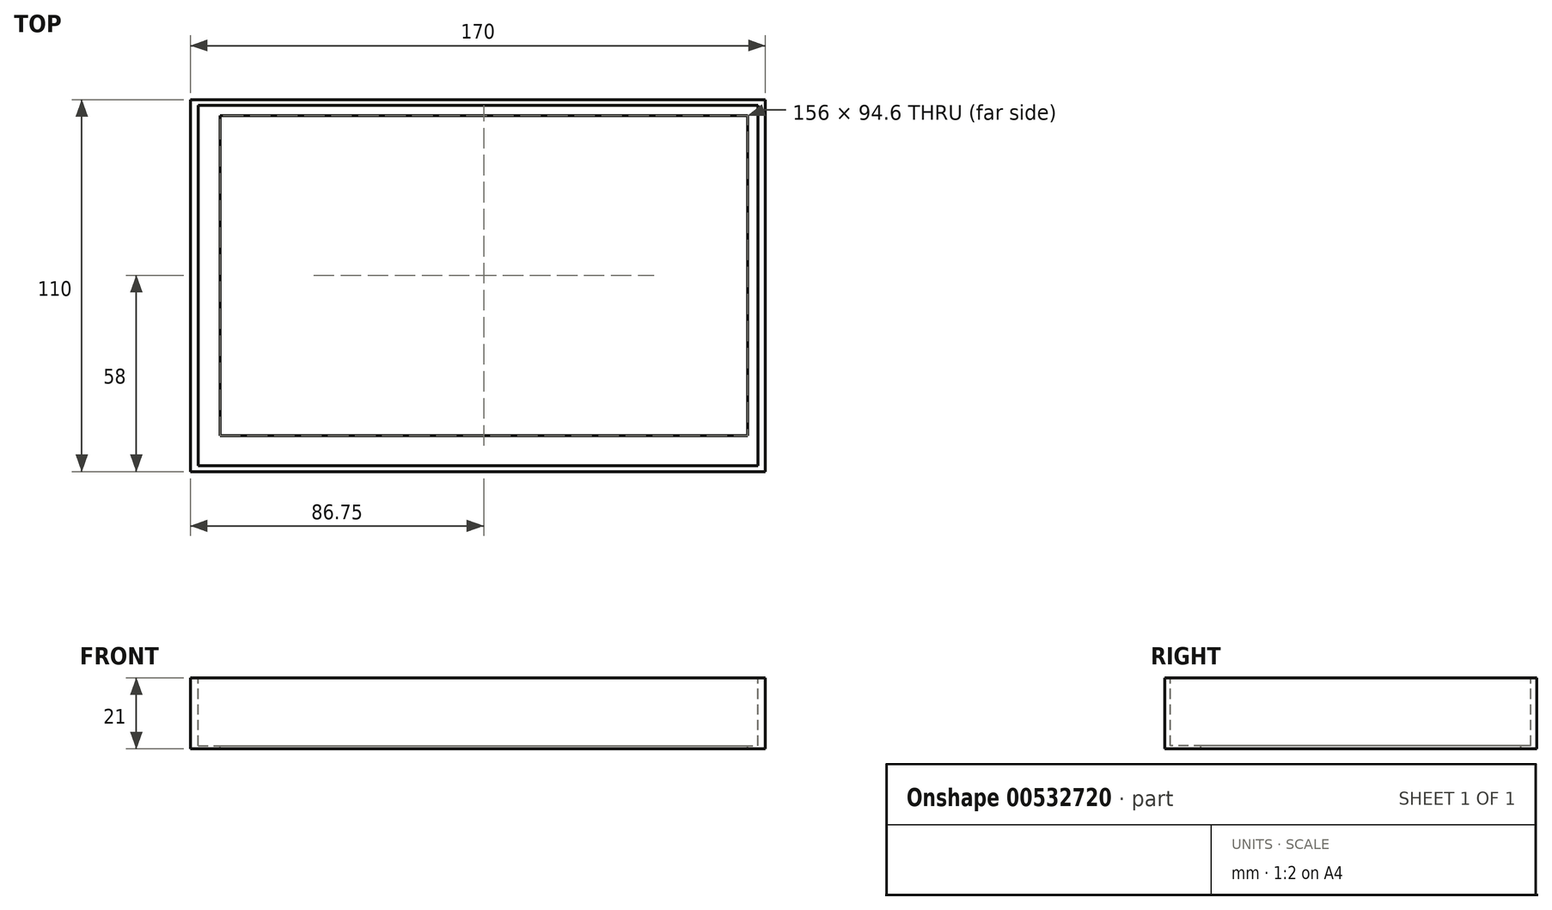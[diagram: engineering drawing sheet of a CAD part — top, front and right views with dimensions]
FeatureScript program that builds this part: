
annotation { "Feature Type Name" : "Feature", "Feature Type Description" : "" }
export const myFeature = defineFeature(function(context is Context, id is Id, definition is map)
    precondition{}
    {
        {
            var Q0;
            Q0=qCreatedBy(makeId("Top.planeOp"),FACE);
            var sketch = newSketch(context, id + "F0", { "sketchPlane" : qUnion([Q0])});
            skLineSegment(sketch, "E0.bottom", {"start": v(85, -55) * mm, "end": v(-85, -55) * mm});
            skLineSegment(sketch, "E0.top", {"start": v(85, 55) * mm, "end": v(-85, 55) * mm});
            skLineSegment(sketch, "E0.left", {"start": v(85, -55) * mm, "end": v(85, 55) * mm});
            skLineSegment(sketch, "E0.right", {"start": v(-85, -55) * mm, "end": v(-85, 55) * mm});
            skPoint(sketch, "E0.middle", {"position": v(0, 0) * mm});
            skSolve(sketch);
        }
        {
            var Q0;
            Q0=makeQuery(id+"F0.imprint","IMPRINT",FACE,{"disambiguationData":[TD([[makeQuery(id+"F0.imprint","IMPRINT",EDGE,{"derivedFrom":sQuery(id+"F0.wireOp",EDGE,"E0.bottom")}),-1.0]])]});
            extrude(context, id + "F1", {"entities" : qUnion([Q0]), "depth" : 21 * mm, "offsetDistance" : 25 * mm});
        }
        {
            var Q0;
            Q0=makeQuery(id+"F1.opExtrude","CAP_FACE",FACE,{"disambiguationData":[OSD([sQuery(id+"F0.wireOp",EDGE,"E0.bottom"),sQuery(id+"F0.wireOp",EDGE,"E0.top"),sQuery(id+"F0.wireOp",EDGE,"E0.left"),sQuery(id+"F0.wireOp",EDGE,"E0.right")])],"isStart":false});
            var sketch = newSketch(context, id + "F2", { "sketchPlane" : qUnion([Q0])});
            skLineSegment(sketch, "E1.bottom", {"start": v(-82.75, 53.3) * mm, "end": v(82.75, 53.3) * mm});
            skLineSegment(sketch, "E1.top", {"start": v(-82.75, -53.3) * mm, "end": v(82.75, -53.3) * mm});
            skLineSegment(sketch, "E1.left", {"start": v(-82.75, 53.3) * mm, "end": v(-82.75, -53.3) * mm});
            skLineSegment(sketch, "E1.right", {"start": v(82.75, 53.3) * mm, "end": v(82.75, -53.3) * mm});
            skSolve(sketch);
        }
        {
            var Q0;
            Q0=makeQuery(id+"F2.imprint","IMPRINT",FACE,{"disambiguationData":[TD([[makeQuery(id+"F2.imprint","IMPRINT",EDGE,{"derivedFrom":sQuery(id+"F2.wireOp",EDGE,"E1.bottom")}),-1.0]])]});
            extrude(context, id + "F3", {"entities" : qUnion([Q0]), "operationType" : NewBodyOperationType.REMOVE, "oppositeDirection" : true, "depth" : 20 * mm, "offsetDistance" : 25 * mm});
        }
        {
            var Q0;
            Q0=makeQuery(id+"F3.boolean.opBoolean","COPY",FACE,{"derivedFrom":makeQuery(id+"F3.opExtrude","CAP_FACE",FACE,{"disambiguationData":[OSD([sQuery(id+"F2.wireOp",EDGE,"E1.bottom"),sQuery(id+"F2.wireOp",EDGE,"E1.top"),sQuery(id+"F2.wireOp",EDGE,"E1.left"),sQuery(id+"F2.wireOp",EDGE,"E1.right")])],"isStart":false})});
            var sketch = newSketch(context, id + "F4", { "sketchPlane" : qUnion([Q0])});
            skLineSegment(sketch, "E2.bottom", {"start": v(-76.25, 50.3) * mm, "end": v(79.75, 50.3) * mm});
            skLineSegment(sketch, "E2.top", {"start": v(-76.25, -44.3) * mm, "end": v(79.75, -44.3) * mm});
            skLineSegment(sketch, "E2.left", {"start": v(-76.25, 50.3) * mm, "end": v(-76.25, -44.3) * mm});
            skLineSegment(sketch, "E2.right", {"start": v(79.75, 50.3) * mm, "end": v(79.75, -44.3) * mm});
            skSolve(sketch);
        }
        {
            var Q0;
            Q0=makeQuery(id+"F4.imprint","IMPRINT",FACE,{"disambiguationData":[TD([[makeQuery(id+"F4.imprint","IMPRINT",EDGE,{"derivedFrom":sQuery(id+"F4.wireOp",EDGE,"E2.bottom")}),-1.0]])]});
            extrude(context, id + "F5", {"entities" : qUnion([Q0]), "operationType" : NewBodyOperationType.REMOVE, "endBound" : BoundingType.THROUGH_ALL, "oppositeDirection" : true, "depth" : 25 * mm, "offsetDistance" : 25 * mm});
        }
    });
